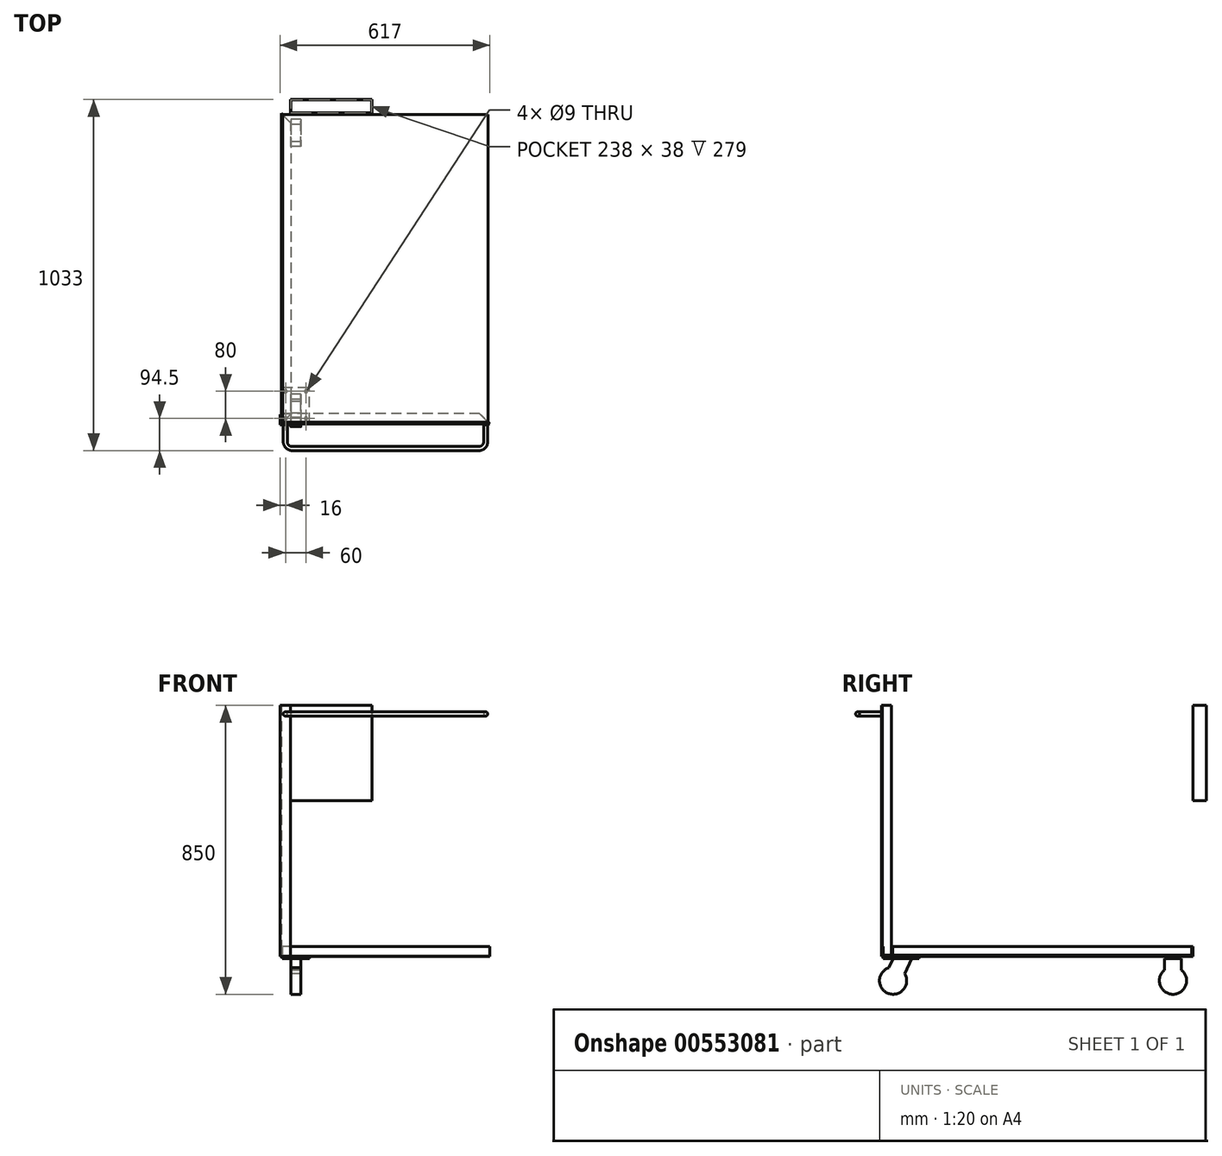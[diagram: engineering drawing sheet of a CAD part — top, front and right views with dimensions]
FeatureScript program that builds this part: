
annotation { "Feature Type Name" : "Feature", "Feature Type Description" : "" }
export const myFeature = defineFeature(function(context is Context, id is Id, definition is map)
    precondition{}
    {
        {
            assignVariable(context, id + "F0", {"name" : "Length", "anyValue" : 920});
        }
        {
            assignVariable(context, id + "F1", {"name" : "Width", "anyValue" : 620});
        }
        {
            assignVariable(context, id + "F2", {"name" : "Hight", "anyValue" : 850});
        }
        {
            assignVariable(context, id + "F3", {"name" : "ProfileThickness", "anyValue" : 3});
        }
        {
            assignVariable(context, id + "F4", {"name" : "CastorMountThickness", "anyValue" : 6});
        }
        {
            assignVariable(context, id + "F5", {"name" : "CastorHight", "anyValue" : 105});
        }
        {
            var Q0;
            Q0=qCreatedBy(makeId("Front.planeOp"),FACE);
            var sketch = newSketch(context, id + "F6", { "sketchPlane" : qUnion([Q0])});
            skLineSegment(sketch, "E0", {"start": v(0, 5) * mm, "end": v(0, 30) * mm});
            skLineSegment(sketch, "E1", {"start": v(0, 30) * mm, "end": v(3, 30) * mm});
            skLineSegment(sketch, "E2", {"start": v(3, 30) * mm, "end": v(3, 5) * mm});
            skLineSegment(sketch, "E3", {"start": v(5, 3) * mm, "end": v(30, 3) * mm});
            skLineSegment(sketch, "E4", {"start": v(30, 3) * mm, "end": v(30, 0) * mm});
            skLineSegment(sketch, "E5", {"start": v(30, 0) * mm, "end": v(5, 0) * mm});
            skPoint(sketch, "E6.visualSharp", {"position": v(0, 0) * mm});
            skArc(sketch, "E6.filletArc", {"start": v(0, 5) * mm, "mid": v(1.46, 1.46) * mm, "end": v(5, 0) * mm});
            skPoint(sketch, "E7.visualSharp", {"position": v(3, 3) * mm});
            skArc(sketch, "E7.filletArc", {"start": v(3, 5) * mm, "mid": v(3.59, 3.59) * mm, "end": v(5, 3) * mm});
            skLineSegment(sketch, "E8", {"start": v(0, 5) * mm, "end": v(0, 0) * mm});
            skLineSegment(sketch, "E9", {"start": v(3, 5) * mm, "end": v(3, 3) * mm});
            skLineSegment(sketch, "E10", {"start": v(5, 3) * mm, "end": v(3, 3) * mm});
            skLineSegment(sketch, "E11", {"start": v(0, 0) * mm, "end": v(5, 0) * mm});
            skSolve(sketch);
        }
        {
            var Q0;
            Q0=makeQuery(id+"F6.imprint","IMPRINT",FACE,{"disambiguationData":[TD([[makeQuery(id+"F6.imprint","IMPRINT",EDGE,{"derivedFrom":sQuery(id+"F6.wireOp",EDGE,"E6.filletArc")}),-1.0]])]});
            var Q1;
            Q1=makeQuery(id+"F6.imprint","IMPRINT",FACE,{"disambiguationData":[TD([[makeQuery(id+"F6.imprint","IMPRINT",EDGE,{"derivedFrom":sQuery(id+"F6.wireOp",EDGE,"E0")}),-1.0]])]});
            extrude(context, id + "F7", {"entities" : qUnion([Q0, Q1]), "depth" : ((getVariable(context, 'Length')) - (getVariable(context, 'ProfileThickness') * 2)) * mm, "symmetric" : true});
        }
        {
            var Q0;
            Q0=qCreatedBy(makeId("Top.planeOp"),FACE);
            var sketch = newSketch(context, id + "F8", { "sketchPlane" : qUnion([Q0])});
            skLineSegment(sketch, "E12", {"start": v(0, -457) * mm, "end": v(30, -427) * mm});
            skLineSegment(sketch, "E13", {"start": v(30, -427) * mm, "end": v(30, -457) * mm});
            skLineSegment(sketch, "E14", {"start": v(30, -457) * mm, "end": v(0, -457) * mm});
            skLineSegment(sketch, "E15", {"start": v(0, 0) * mm, "end": v(30, 0) * mm, "construction": true});
            skLineSegment(sketch, "E16.MirrorCS", {"start": v(30, 427) * mm, "end": v(30, 457) * mm});
            skLineSegment(sketch, "E17.MirrorCS", {"start": v(30, 457) * mm, "end": v(0, 457) * mm});
            skLineSegment(sketch, "E18.MirrorCS", {"start": v(0, 457) * mm, "end": v(30, 427) * mm});
            skSolve(sketch);
        }
        {
            var Q0;
            Q0=qSketchRegion(id+"F8",true);
            var Q1;
            Q1=makeQuery(id+"F7.opExtrude","SWEPT_FACE",FACE,{"disambiguationData":[OSD([sQuery(id+"F6.wireOp",EDGE,"E1")])]});
            extrude(context, id + "F9", {"entities" : qUnion([Q0]), "operationType" : NewBodyOperationType.REMOVE, "endBound" : BoundingType.UP_TO_SURFACE, "endBoundEntityFace" : qUnion([Q1]), "depth" : 25 * mm});
        }
        {
            var Q0;
            Q0=qCreatedBy(makeId("Right.planeOp"),FACE);
            var sketch = newSketch(context, id + "F10", { "sketchPlane" : qUnion([Q0])});
            skLineSegment(sketch, "E19", {"start": v(-457, 5) * mm, "end": v(-457, 30) * mm});
            skLineSegment(sketch, "E20", {"start": v(-457, 30) * mm, "end": v(-454, 30) * mm});
            skLineSegment(sketch, "E21", {"start": v(-454, 30) * mm, "end": v(-454, 5) * mm});
            skLineSegment(sketch, "E22", {"start": v(-452, 3) * mm, "end": v(-427, 3) * mm});
            skLineSegment(sketch, "E23", {"start": v(-427, 3) * mm, "end": v(-427, 0) * mm});
            skLineSegment(sketch, "E24", {"start": v(-427, 0) * mm, "end": v(-452, 0) * mm});
            skPoint(sketch, "E25.visualSharp", {"position": v(-457, 0) * mm});
            skArc(sketch, "E25.filletArc", {"start": v(-457, 5) * mm, "mid": v(-455.54, 1.46) * mm, "end": v(-452, 0) * mm});
            skPoint(sketch, "E26.visualSharp", {"position": v(-454, 3) * mm});
            skArc(sketch, "E26.filletArc", {"start": v(-454, 5) * mm, "mid": v(-453.41, 3.59) * mm, "end": v(-452, 3) * mm});
            skLineSegment(sketch, "E27", {"start": v(-452, 0) * mm, "end": v(-457, 0) * mm});
            skLineSegment(sketch, "E28", {"start": v(-457, 5) * mm, "end": v(-457, 0) * mm});
            skLineSegment(sketch, "E29", {"start": v(-452, 3) * mm, "end": v(-454, 3) * mm});
            skLineSegment(sketch, "E30", {"start": v(-454, 5) * mm, "end": v(-454, 3) * mm});
            skSolve(sketch);
        }
        {
            var Q0;
            Q0=makeQuery(id+"F10.imprint","IMPRINT",FACE,{"disambiguationData":[TD([[makeQuery(id+"F10.imprint","IMPRINT",EDGE,{"derivedFrom":sQuery(id+"F10.wireOp",EDGE,"E25.filletArc")}),-1.0]])]});
            var Q1;
            Q1=makeQuery(id+"F10.imprint","IMPRINT",FACE,{"disambiguationData":[TD([[makeQuery(id+"F10.imprint","IMPRINT",EDGE,{"derivedFrom":sQuery(id+"F10.wireOp",EDGE,"E19")}),-1.0]])]});
            extrude(context, id + "F11", {"entities" : qUnion([Q0, Q1]), "depth" : (((getVariable(context, 'Width')) - (getVariable(context, 'ProfileThickness') * 2))) * mm});
        }
        {
            var Q0;
            Q0=qCreatedBy(makeId("Top.planeOp"),FACE);
            var sketch = newSketch(context, id + "F12", { "sketchPlane" : qUnion([Q0])});
            skLineSegment(sketch, "E31", {"start": v(30, -427) * mm, "end": v(0, -457) * mm});
            skLineSegment(sketch, "E32", {"start": v(0, -427) * mm, "end": v(0, -457) * mm});
            skLineSegment(sketch, "E33", {"start": v(307, -457) * mm, "end": v(307, -427) * mm, "construction": true});
            skLineSegment(sketch, "E34", {"start": v(30, -427) * mm, "end": v(0, -427) * mm});
            skLineSegment(sketch, "E35.MirrorCS", {"start": v(584, -427) * mm, "end": v(614, -457) * mm});
            skLineSegment(sketch, "E36.MirrorCS", {"start": v(584, -427) * mm, "end": v(614, -427) * mm});
            skLineSegment(sketch, "E37.MirrorCS", {"start": v(614, -427) * mm, "end": v(614, -457) * mm});
            skSolve(sketch);
        }
        {
            var Q0;
            Q0=qSketchRegion(id+"F12",true);
            var Q1;
            Q1=makeQuery(id+"F11.opExtrude","SWEPT_FACE",FACE,{"disambiguationData":[OSD([sQuery(id+"F10.wireOp",EDGE,"E20")])]});
            extrude(context, id + "F13", {"entities" : qUnion([Q0]), "operationType" : NewBodyOperationType.REMOVE, "endBound" : BoundingType.UP_TO_SURFACE, "endBoundEntityFace" : qUnion([Q1]), "depth" : 25 * mm});
        }
        {
            var Q0;
            Q0=qCreatedBy(makeId("Top.planeOp"),FACE);
            var sketch = newSketch(context, id + "F14", { "sketchPlane" : qUnion([Q0])});
            skLineSegment(sketch, "E38", {"start": v(-3, -455) * mm, "end": v(-3, -430) * mm});
            skLineSegment(sketch, "E39", {"start": v(-3, -430) * mm, "end": v(0, -430) * mm});
            skLineSegment(sketch, "E40", {"start": v(0, -430) * mm, "end": v(0, -455) * mm});
            skLineSegment(sketch, "E41", {"start": v(2, -457) * mm, "end": v(27, -457) * mm});
            skLineSegment(sketch, "E42", {"start": v(27, -457) * mm, "end": v(27, -460) * mm});
            skLineSegment(sketch, "E43", {"start": v(27, -460) * mm, "end": v(2, -460) * mm});
            skPoint(sketch, "E44.visualSharp", {"position": v(-3, -460) * mm});
            skArc(sketch, "E44.filletArc", {"start": v(-3, -455) * mm, "mid": v(-1.54, -458.54) * mm, "end": v(2, -460) * mm});
            skPoint(sketch, "E45.visualSharp", {"position": v(0, -457) * mm});
            skArc(sketch, "E45.filletArc", {"start": v(0, -455) * mm, "mid": v(0.59, -456.41) * mm, "end": v(2, -457) * mm});
            skLineSegment(sketch, "E46", {"start": v(-3, -455) * mm, "end": v(-3, -460) * mm});
            skLineSegment(sketch, "E47", {"start": v(-3, -460) * mm, "end": v(2, -460) * mm});
            skLineSegment(sketch, "E48", {"start": v(0, -455) * mm, "end": v(0, -457) * mm});
            skLineSegment(sketch, "E49", {"start": v(2, -457) * mm, "end": v(0, -457) * mm});
            skSolve(sketch);
        }
        {
            var Q0;
            Q0=makeQuery(id+"F14.imprint","IMPRINT",FACE,{"disambiguationData":[TD([[makeQuery(id+"F14.imprint","IMPRINT",EDGE,{"derivedFrom":sQuery(id+"F14.wireOp",EDGE,"E44.filletArc")}),-1.0]])]});
            var Q1;
            Q1=makeQuery(id+"F14.imprint","IMPRINT",FACE,{"disambiguationData":[TD([[makeQuery(id+"F14.imprint","IMPRINT",EDGE,{"derivedFrom":sQuery(id+"F14.wireOp",EDGE,"E38")}),-1.0]])]});
            extrude(context, id + "F15", {"entities" : qUnion([Q0, Q1]), "depth" : (getVariable(context, 'Hight') - getVariable(context, 'CastorMountThickness') - getVariable(context, 'CastorHight')) * mm});
        }
        {
            var Q0;
            Q0=qCreatedBy(makeId("Top.planeOp"),FACE);
            var sketch = newSketch(context, id + "F16", { "sketchPlane" : qUnion([Q0])});
            skLineSegment(sketch, "E50.bottom", {"start": v(3, -454) * mm, "end": v(83, -454) * mm});
            skLineSegment(sketch, "E50.top", {"start": v(3, -349) * mm, "end": v(83, -349) * mm});
            skLineSegment(sketch, "E50.left", {"start": v(3, -454) * mm, "end": v(3, -349) * mm});
            skLineSegment(sketch, "E50.right", {"start": v(83, -454) * mm, "end": v(83, -349) * mm});
            skSolve(sketch);
        }
        {
            var Q0;
            Q0=qSketchRegion(id+"F16",true);
            extrude(context, id + "F17", {"entities" : qUnion([Q0]), "oppositeDirection" : true, "depth" : (getVariable(context, 'CastorMountThickness')) * mm});
        }
        {
            var Q0;
            Q0=makeQuery(id+"F17.opExtrude","CAP_FACE",FACE,{"disambiguationData":[OSD([sQuery(id+"F16.wireOp",EDGE,"E50.bottom"),sQuery(id+"F16.wireOp",EDGE,"E50.top"),sQuery(id+"F16.wireOp",EDGE,"E50.left"),sQuery(id+"F16.wireOp",EDGE,"E50.right")])],"isStart":false});
            var sketch = newSketch(context, id + "F18", { "sketchPlane" : qUnion([Q0])});
            skLineSegment(sketch, "E51", {"start": v(3, 401.5) * mm, "end": v(83, 401.5) * mm, "construction": true});
            skLineSegment(sketch, "E52", {"start": v(43, 349) * mm, "end": v(43, 454) * mm, "construction": true});
            skPoint(sketch, "E53", {"position": v(13, 441.5) * mm});
            skPoint(sketch, "E54", {"position": v(73, 441.5) * mm});
            skPoint(sketch, "E55", {"position": v(73, 361.5) * mm});
            skPoint(sketch, "E56", {"position": v(13, 361.5) * mm});
            skLineSegment(sketch, "E57", {"start": v(13, 441.5) * mm, "end": v(73, 441.5) * mm, "construction": true});
            skLineSegment(sketch, "E58", {"start": v(73, 361.5) * mm, "end": v(73, 441.5) * mm, "construction": true});
            skSolve(sketch);
        }
        {
            var Q0;
            Q0=sQuery(id+"F18.wireOp",VERTEX,"E53");
            var Q1;
            Q1=sQuery(id+"F18.wireOp",VERTEX,"E54");
            var Q2;
            Q2=sQuery(id+"F18.wireOp",VERTEX,"E55");
            var Q3;
            Q3=sQuery(id+"F18.wireOp",VERTEX,"E56");
            var Q4;
            Q4=makeQuery(id+"F17.opExtrude","SWEPT_BODY",BODY,{"disambiguationData":[OSD([sQuery(id+"F16.wireOp",EDGE,"E50.bottom"),sQuery(id+"F16.wireOp",EDGE,"E50.top"),sQuery(id+"F16.wireOp",EDGE,"E50.left"),sQuery(id+"F16.wireOp",EDGE,"E50.right")])]});
            hole(context, id + "F19", {"style" : HoleStyle.SIMPLE, "endStyle" : HoleEndStyle.THROUGH, "holeDiameter" : 9 * mm, "isTappedThrough" : true, "tappedDepth" : 16 * mm, "tapClearance" : 3, "startFromSketch" : true, "locations" : qUnion([Q0, Q1, Q2, Q3]), "scope" : qUnion([Q4])});
        }
        {
            var Q0;
            Q0=makeQuery(id+"F15.opExtrude","CAP_FACE",FACE,{"disambiguationData":[OSD([sQuery(id+"F14.wireOp",EDGE,"E38"),sQuery(id+"F14.wireOp",EDGE,"E39"),sQuery(id+"F14.wireOp",EDGE,"E40"),sQuery(id+"F14.wireOp",EDGE,"E41"),sQuery(id+"F14.wireOp",EDGE,"E42"),sQuery(id+"F14.wireOp",EDGE,"E43"),sQuery(id+"F14.wireOp",EDGE,"E46"),sQuery(id+"F14.wireOp",EDGE,"E47"),sQuery(id+"F14.wireOp",EDGE,"E48"),sQuery(id+"F14.wireOp",EDGE,"E49")])],"isStart":false});
            cPlane(context, id + "F20", {"entities" : qUnion([Q0]), "cplaneType" : CPlaneType.OFFSET, "offset" : 25 * mm, "oppositeDirection" : true, "width" : 150 * mm, "height" : 150 * mm});
        }
        {
            var Q0;
            Q0=qCreatedBy(id+"F20.planeOp",FACE);
            var sketch = newSketch(context, id + "F21", { "sketchPlane" : qUnion([Q0])});
            skLineSegment(sketch, "E59", {"start": v(12, -460) * mm, "end": v(12, -510) * mm});
            skLineSegment(sketch, "E60", {"start": v(32, -530) * mm, "end": v(582, -530) * mm});
            skLineSegment(sketch, "E61", {"start": v(602, -510) * mm, "end": v(602, -460) * mm});
            skPoint(sketch, "E62.visualSharp", {"position": v(12, -530) * mm});
            skArc(sketch, "E62.filletArc", {"start": v(12, -510) * mm, "mid": v(17.86, -524.14) * mm, "end": v(32, -530) * mm});
            skPoint(sketch, "E63.visualSharp", {"position": v(602, -530) * mm});
            skArc(sketch, "E63.filletArc", {"start": v(582, -530) * mm, "mid": v(596.14, -524.14) * mm, "end": v(602, -510) * mm});
            skSolve(sketch);
        }
        {
            var Q0;
            Q0=makeQuery(id+"F15.opExtrude","SWEPT_FACE",FACE,{"disambiguationData":[OSD([sQuery(id+"F14.wireOp",EDGE,"E43"),sQuery(id+"F14.wireOp",EDGE,"E47")])]});
            var sketch = newSketch(context, id + "F22", { "sketchPlane" : qUnion([Q0])});
            skCircle(sketch, "E64", {"center": v(12, 714) * mm, "radius": 6 * mm});
            skSolve(sketch);
        }
        {
            var Q0;
            Q0=makeQuery(id+"F22.imprint","IMPRINT",FACE,{"disambiguationData":[TD([[makeQuery(id+"F22.imprint","IMPRINT",EDGE,{"derivedFrom":sQuery(id+"F22.wireOp",EDGE,"E64")}),1.0]])]});
            var Q1;
            Q1=sQuery(id+"F21.wireOp",EDGE,"E59");
            var Q2;
            Q2=sQuery(id+"F21.wireOp",EDGE,"E62.filletArc");
            var Q3;
            Q3=sQuery(id+"F21.wireOp",EDGE,"E60");
            var Q4;
            Q4=sQuery(id+"F21.wireOp",EDGE,"E63.filletArc");
            var Q5;
            Q5=sQuery(id+"F21.wireOp",EDGE,"E61");
            sweep(context, id + "F23", {"profiles" : qUnion([Q0]), "path" : qUnion([Q1, Q2, Q3, Q4, Q5])});
        }
        {
            var Q0;
            Q0=makeQuery(id+"F9.boolean.opBoolean","MERGE",EDGE,{"derivedFrom":[makeQuery(id+"F7.opExtrude","CAP_EDGE",EDGE,{"disambiguationData":[OSD([sQuery(id+"F6.wireOp",EDGE,"E0"),sQuery(id+"F6.wireOp",EDGE,"E8")])],"isStart":true}),makeQuery(id+"F9.opExtrude","SWEPT_EDGE",EDGE,{"disambiguationData":[OSD([sQuery(id+"F8.wireOp",EDGE,"E17.MirrorCS"),sQuery(id+"F8.wireOp",EDGE,"E18.MirrorCS")])]})]});
            cPlane(context, id + "F24", {"entities" : qUnion([Q0]), "cplaneType" : CPlaneType.LINE_ANGLE, "offset" : 25 * mm, "angle" : 90 * degree, "width" : 150 * mm, "height" : 150 * mm});
        }
        {
            var Q0;
            Q0=qCreatedBy(id+"F24.planeOp",FACE);
            var sketch = newSketch(context, id + "F25", { "sketchPlane" : qUnion([Q0])});
            skLineSegment(sketch, "E65.bottom", {"start": v(-267, 739) * mm, "end": v(-27, 739) * mm});
            skLineSegment(sketch, "E65.top", {"start": v(-267, 459) * mm, "end": v(-27, 459) * mm});
            skLineSegment(sketch, "E65.left", {"start": v(-267, 739) * mm, "end": v(-267, 459) * mm});
            skLineSegment(sketch, "E65.right", {"start": v(-27, 739) * mm, "end": v(-27, 459) * mm});
            skSolve(sketch);
        }
        {
            var Q0;
            Q0=qSketchRegion(id+"F25",true);
            extrude(context, id + "F26", {"entities" : qUnion([Q0]), "depth" : 40 * mm});
        }
        {
            var Q0;
            Q0=makeQuery(id+"F26.opExtrude","SWEPT_FACE",FACE,{"disambiguationData":[OSD([sQuery(id+"F25.wireOp",EDGE,"E65.bottom")])]});
            shell(context, id + "F27", {"entities" : qUnion([Q0]), "thickness" : 1 * mm});
        }
        {
            var Q0;
            Q0=qCreatedBy(makeId("Right.planeOp"),FACE);
            var sketch = newSketch(context, id + "F28", { "sketchPlane" : qUnion([Q0])});
            skArc(sketch, "E66", {"start": v(-431.15, -41.46) * mm, "mid": v(-410, -111) * mm, "end": v(-388.85, -41.46) * mm});
            skLineSegment(sketch, "E67.top", {"start": v(-431.15, -6) * mm, "end": v(-388.85, -6) * mm});
            skLineSegment(sketch, "E67.left", {"start": v(-431.15, -41.46) * mm, "end": v(-431.15, -6) * mm});
            skLineSegment(sketch, "E67.right", {"start": v(-388.85, -41.46) * mm, "end": v(-388.85, -6) * mm});
            skSolve(sketch);
        }
        {
            var Q0;
            Q0=makeQuery(id+"F7.opExtrude","SWEPT_FACE",FACE,{"disambiguationData":[OSD([sQuery(id+"F6.wireOp",EDGE,"E3"),sQuery(id+"F6.wireOp",EDGE,"E10")])]});
            var sketch = newSketch(context, id + "F29", { "sketchPlane" : qUnion([Q0])});
            skLineSegment(sketch, "E68.bottom", {"start": v(4.5, -452.5) * mm, "end": v(609.5, -452.5) * mm});
            skLineSegment(sketch, "E68.top", {"start": v(4.5, 452.5) * mm, "end": v(609.5, 452.5) * mm});
            skLineSegment(sketch, "E68.left", {"start": v(4.5, -452.5) * mm, "end": v(4.5, 452.5) * mm});
            skLineSegment(sketch, "E68.right", {"start": v(609.5, -452.5) * mm, "end": v(609.5, 452.5) * mm});
            skSolve(sketch);
        }
        {
            var Q0;
            Q0=qSketchRegion(id+"F29",true);
            extrude(context, id + "F30", {"entities" : qUnion([Q0]), "depth" : 1.5 * mm});
        }
        {
            var Q0;
            Q0=makeQuery(id+"F17.opExtrude","CAP_EDGE",EDGE,{"disambiguationData":[OSD([sQuery(id+"F16.wireOp",EDGE,"E50.left")])],"isStart":false});
            cPoint(context, id + "F31", {"entities" : qUnion([Q0]), "parameter" : 0.5});
        }
        {
            var Q0;
            Q0=makeQuery(id+"F17.opExtrude","CAP_EDGE",EDGE,{"disambiguationData":[OSD([sQuery(id+"F16.wireOp",EDGE,"E50.right")])],"isStart":false});
            cPoint(context, id + "F32", {"entities" : qUnion([Q0]), "parameter" : 0.5});
        }
        {
            var Q0;
            Q0=qCreatedBy(id+"F31",VERTEX);
            var Q1;
            Q1=qCreatedBy(id+"F32",VERTEX);
            cPlane(context, id + "F33", {"entities" : qUnion([Q0, Q1]), "cplaneType" : CPlaneType.MID_PLANE, "offset" : 25 * mm, "width" : 150 * mm, "height" : 150 * mm});
        }
        {
            var Q0;
            Q0=qCreatedBy(id+"F33.planeOp",FACE);
            var sketch = newSketch(context, id + "F34", { "sketchPlane" : qUnion([Q0])});
            skArc(sketch, "E69", {"start": v(373.5, -39.78) * mm, "mid": v(398.5, -111) * mm, "end": v(423.5, -39.78) * mm});
            skLineSegment(sketch, "E70", {"start": v(423.5, -39.78) * mm, "end": v(423.5, -6) * mm});
            skLineSegment(sketch, "E71", {"start": v(423.5, -6) * mm, "end": v(373.5, -6) * mm});
            skLineSegment(sketch, "E72", {"start": v(373.5, -6) * mm, "end": v(373.5, -39.78) * mm});
            skLineSegment(sketch, "E73", {"start": v(398.5, -71) * mm, "end": v(398.5, -6) * mm, "construction": true});
            skSolve(sketch);
        }
        {
            var Q0;
            Q0=qSketchRegion(id+"F34",true);
            extrude(context, id + "F35", {"entities" : qUnion([Q0]), "depth" : 30 * mm, "symmetric" : true});
        }
        {
            var Q0;
            Q0=qCreatedBy(id+"F33.planeOp",FACE);
            var sketch = newSketch(context, id + "F36", { "sketchPlane" : qUnion([Q0])});
            skArc(sketch, "E74", {"start": v(-438.25, -33.09) * mm, "mid": v(-439.35, -108.52) * mm, "end": v(-391.17, -50.47) * mm});
            skLineSegment(sketch, "E75", {"start": v(-425.5, -71) * mm, "end": v(-401.5, -6) * mm, "construction": true});
            skLineSegment(sketch, "E76", {"start": v(-425.5, -71) * mm, "end": v(-425.5, -6) * mm, "construction": true});
            skLineSegment(sketch, "E77", {"start": v(-391.17, -50.47) * mm, "end": v(-370.24, -6) * mm});
            skLineSegment(sketch, "E78", {"start": v(-370.24, -6) * mm, "end": v(-425.5, -6) * mm});
            skLineSegment(sketch, "E79", {"start": v(-425.5, -6) * mm, "end": v(-438.25, -33.09) * mm});
            skSolve(sketch);
        }
        {
            var Q0;
            Q0=qSketchRegion(id+"F36",true);
            extrude(context, id + "F37", {"entities" : qUnion([Q0]), "depth" : 30 * mm, "symmetric" : true});
        }
    });
